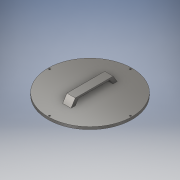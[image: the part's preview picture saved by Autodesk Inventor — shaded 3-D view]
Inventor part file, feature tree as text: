
AUTODESK INVENTOR PART (.ipt)
format: ipt  version: 2017 (Build 210142000, 142)  size: 148,992 bytes
history: native  units: in
note: dims shown in document units (in); Inventor stores cm internally (conversion verified against a paired STEP export)
features: sketch x5, extrude x2, plane x1, loft x1, mirror x1, hole x1, pattern_circular x1
ambient origin geometry x8: Origin, YZ Plane, XZ Plane, XY Plane, X Axis, Y Axis, Z Axis, Center Point
bodies: Solid1 (feature_tree)
feature tree (12):
  extrude  "Extrusion1"  Depth=0.3in TaperAngle=0.0deg
  sketch  "Sketch2"  dims[d4=2.5in d5=0.5in]
  plane  "Work Plane1"
  loft  "Loft1"
  extrude  "Extrusion2"  Depth=0.8in
  mirror  "Mirror1"
  hole  "Hole1"  [1 undecoded]
  pattern_circular  "Circular Pattern1"  Angle=90.0deg  [1 undecoded]
  sketch  "Sketch1"  dims[d0=10.0in d1=0.3in d2=0.0in]
  sketch  "Sketch3"  dims[d6=1.0in d7=0.8in]
  sketch  "Sketch4"  dims[d8=2.0in d9=0.5in]
  sketch  "Sketch5"  dims[d10=1.0in d11=0.0in d12=90.0deg d13=0.0in d14=90.0deg d15=0.1in d16=1.0in d17=0.3in d18=0.0in d19=4.8097in d20=0.196in d21=0.5in d22=0.375in d23=0.25in d24=0.5635in d25=0.75in d26=0.8108in d27=1.5748in d28=360.0deg]
note: 2 required parameter values undecoded (feature->parameter linkage not recoverable at this tier; creation-order binding heuristic only, values carry confidence <= 0.55)
